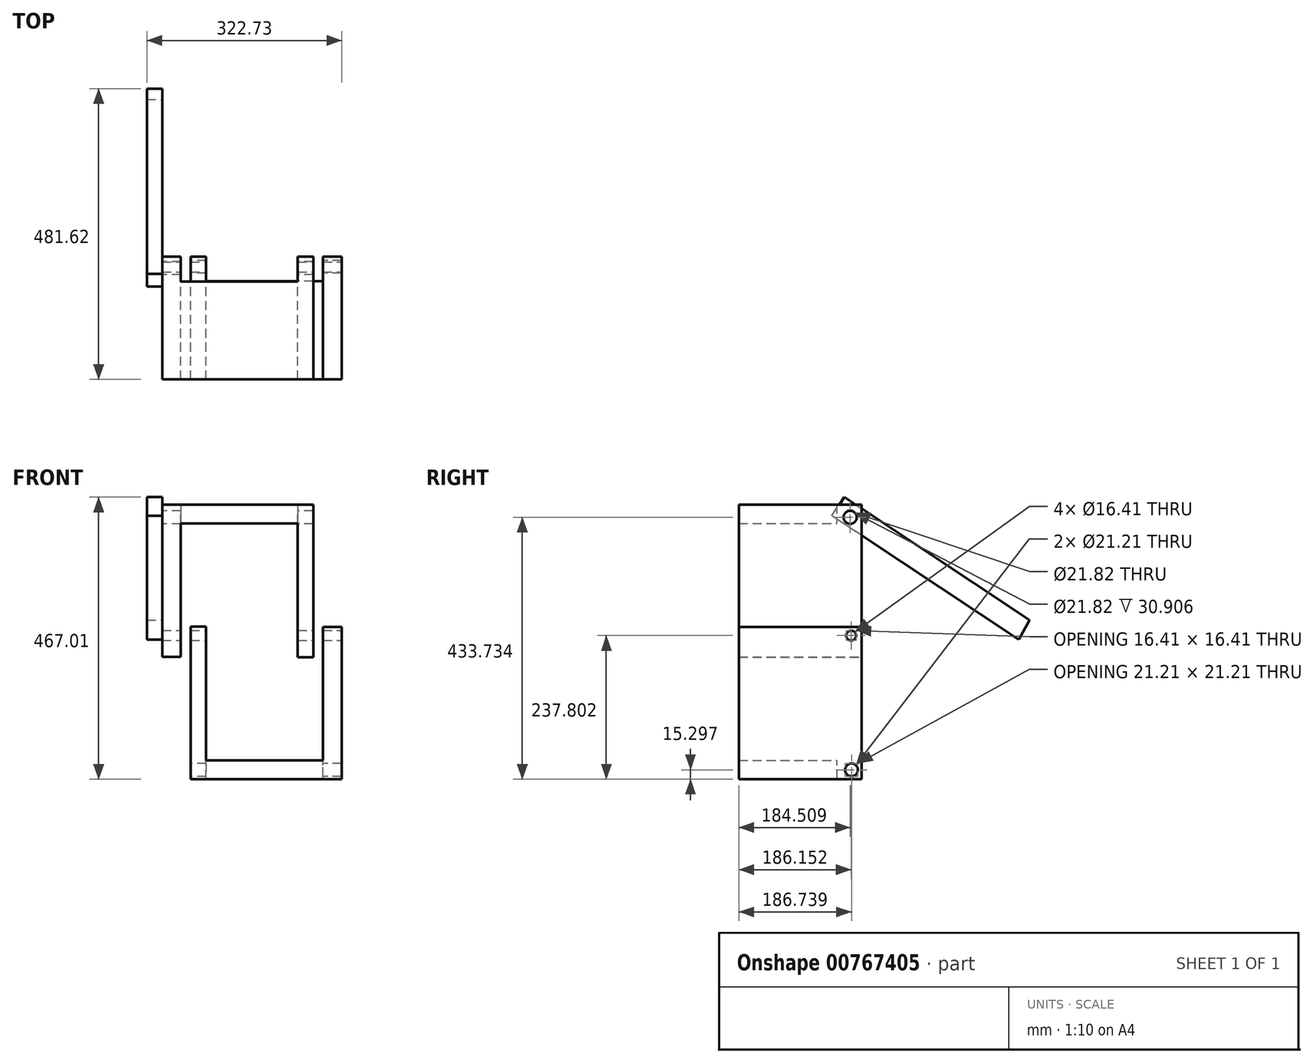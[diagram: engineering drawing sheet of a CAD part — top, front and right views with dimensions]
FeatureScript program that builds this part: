
annotation { "Feature Type Name" : "Feature", "Feature Type Description" : "" }
export const myFeature = defineFeature(function(context is Context, id is Id, definition is map)
    precondition{}
    {
        {
            var Q0;
            Q0=qCreatedBy(makeId("Front.planeOp"),FACE);
            var sketch = newSketch(context, id + "F0", { "sketchPlane" : qUnion([Q0])});
            skLineSegment(sketch, "E0", {"start": v(-82.01, 34.88) * mm, "end": v(-82.01, -217.77) * mm});
            skLineSegment(sketch, "E1", {"start": v(-82.01, -217.77) * mm, "end": v(168.25, -217.77) * mm});
            skLineSegment(sketch, "E2", {"start": v(168.25, -217.77) * mm, "end": v(168.25, 34.28) * mm});
            skLineSegment(sketch, "E3", {"start": v(168.25, 34.28) * mm, "end": v(137.35, 34.28) * mm});
            skLineSegment(sketch, "E4", {"start": v(137.35, 34.28) * mm, "end": v(137.35, -186.86) * mm});
            skLineSegment(sketch, "E5", {"start": v(137.35, -186.86) * mm, "end": v(-56.22, -186.86) * mm});
            skLineSegment(sketch, "E6", {"start": v(-56.22, -186.86) * mm, "end": v(-56.22, 34.88) * mm});
            skLineSegment(sketch, "E7", {"start": v(-56.22, 34.88) * mm, "end": v(-82.01, 34.88) * mm});
            skSolve(sketch);
        }
        {
            var Q0;
            Q0 = qSketchRegion(id + "F0", true);
            extrude(context, id + "F1", {"entities" : qUnion([Q0]), "depth" : 203.2 * mm, "offsetDistance" : 25.4 * mm});
        }
        {
            var Q0;
            Q0=makeQuery(id+"F1.opExtrude","SWEPT_BODY",BODY,{"disambiguationData":[OSD([sQuery(id+"F0.wireOp",EDGE,"E0"),sQuery(id+"F0.wireOp",EDGE,"E1"),sQuery(id+"F0.wireOp",EDGE,"E2"),sQuery(id+"F0.wireOp",EDGE,"E3"),sQuery(id+"F0.wireOp",EDGE,"E4"),sQuery(id+"F0.wireOp",EDGE,"E5"),sQuery(id+"F0.wireOp",EDGE,"E6"),sQuery(id+"F0.wireOp",EDGE,"E7")])]});
            transform(context, id + "F2", {"entities" : qUnion([Q0]), "transformType" : TransformType.TRANSLATION_3D, "dx" : 254 * mm, "dy" : 0 * mm, "dz" : 0 * mm, "makeCopy" : true});
        }
        {
            var Q0;
            Q0=makeQuery(id+"F2.opPattern","COPY",BODY,{"derivedFrom":makeQuery(id+"F1.opExtrude","SWEPT_BODY",BODY,{"disambiguationData":[OSD([sQuery(id+"F0.wireOp",EDGE,"E0"),sQuery(id+"F0.wireOp",EDGE,"E1"),sQuery(id+"F0.wireOp",EDGE,"E2"),sQuery(id+"F0.wireOp",EDGE,"E3"),sQuery(id+"F0.wireOp",EDGE,"E4"),sQuery(id+"F0.wireOp",EDGE,"E5"),sQuery(id+"F0.wireOp",EDGE,"E6"),sQuery(id+"F0.wireOp",EDGE,"E7")])]}),"instanceName":"1"});
            var Q1;
            Q1=makeQuery(id+"F2.opPattern","COPY",EDGE,{"derivedFrom":makeQuery(id+"F1.opExtrude","SWEPT_EDGE",EDGE,{"disambiguationData":[OSD([sQuery(id+"F0.wireOp",EDGE,"E0"),sQuery(id+"F0.wireOp",EDGE,"E7")])]}),"instanceName":"1"});
            transform(context, id + "F3", {"entities" : qUnion([Q0]), "transformType" : TransformType.ROTATION, "transformAxis" : qUnion([Q1]), "angle" : 180 * degree, "makeCopy" : false});
        }
        {
            var Q0;
            Q0=makeQuery(id+"F2.opPattern","COPY",BODY,{"derivedFrom":makeQuery(id+"F1.opExtrude","SWEPT_BODY",BODY,{"disambiguationData":[OSD([sQuery(id+"F0.wireOp",EDGE,"E0"),sQuery(id+"F0.wireOp",EDGE,"E1"),sQuery(id+"F0.wireOp",EDGE,"E2"),sQuery(id+"F0.wireOp",EDGE,"E3"),sQuery(id+"F0.wireOp",EDGE,"E4"),sQuery(id+"F0.wireOp",EDGE,"E5"),sQuery(id+"F0.wireOp",EDGE,"E6"),sQuery(id+"F0.wireOp",EDGE,"E7")])]}),"instanceName":"1"});
            var Q1;
            Q1=makeQuery(id+"F2.opPattern","COPY",EDGE,{"derivedFrom":makeQuery(id+"F1.opExtrude","CAP_EDGE",EDGE,{"disambiguationData":[OSD([sQuery(id+"F0.wireOp",EDGE,"E6")])],"isStart":true}),"instanceName":"1"});
            var Q2;
            Q2=makeQuery(id+"F2.opPattern","COPY",EDGE,{"derivedFrom":makeQuery(id+"F1.opExtrude","CAP_EDGE",EDGE,{"disambiguationData":[OSD([sQuery(id+"F0.wireOp",EDGE,"E6")])],"isStart":true}),"instanceName":"1"});
            transform(context, id + "F4", {"entities" : qUnion([Q0]), "transformType" : TransformType.TRANSLATION_DISTANCE, "transformDirection" : qUnion([Q2]), "distance" : 50.8 * mm, "makeCopy" : false});
        }
        {
            var Q0;
            Q0=makeQuery(id+"F2.opPattern","COPY",BODY,{"derivedFrom":makeQuery(id+"F1.opExtrude","SWEPT_BODY",BODY,{"disambiguationData":[OSD([sQuery(id+"F0.wireOp",EDGE,"E0"),sQuery(id+"F0.wireOp",EDGE,"E1"),sQuery(id+"F0.wireOp",EDGE,"E2"),sQuery(id+"F0.wireOp",EDGE,"E3"),sQuery(id+"F0.wireOp",EDGE,"E4"),sQuery(id+"F0.wireOp",EDGE,"E5"),sQuery(id+"F0.wireOp",EDGE,"E6"),sQuery(id+"F0.wireOp",EDGE,"E7")])]}),"instanceName":"1"});
            var Q1;
            Q1=makeQuery(id+"F2.opPattern","COPY",EDGE,{"derivedFrom":makeQuery(id+"F1.opExtrude","CAP_EDGE",EDGE,{"disambiguationData":[OSD([sQuery(id+"F0.wireOp",EDGE,"E1")])],"isStart":true}),"instanceName":"1"});
            transform(context, id + "F5", {"entities" : qUnion([Q0]), "transformType" : TransformType.TRANSLATION_DISTANCE, "transformDirection" : qUnion([Q1]), "distance" : 50.8 * mm, "makeCopy" : false});
        }
        {
            var Q0;
            Q0=makeQuery(id+"F1.opExtrude","SWEPT_FACE",FACE,{"disambiguationData":[OSD([sQuery(id+"F0.wireOp",EDGE,"E2")])]});
            var sketch = newSketch(context, id + "F6", { "sketchPlane" : qUnion([Q0])});
            skCircle(sketch, "E8", {"center": v(-17.05, 20.03) * mm, "radius": 8.2 * mm});
            skSolve(sketch);
        }
        {
            var Q0;
            Q0 = qSketchRegion(id + "F6", true);
            extrude(context, id + "F7", {"entities" : qUnion([Q0]), "operationType" : NewBodyOperationType.REMOVE, "endBound" : BoundingType.THROUGH_ALL, "oppositeDirection" : true, "depth" : 25.4 * mm, "offsetDistance" : 25.4 * mm});
        }
        {
            var Q0;
            Q0=makeQuery(id+"F2.opPattern","COPY",FACE,{"derivedFrom":makeQuery(id+"F1.opExtrude","SWEPT_FACE",FACE,{"disambiguationData":[OSD([sQuery(id+"F0.wireOp",EDGE,"E5")])]}),"instanceName":"1"});
            var sketch = newSketch(context, id + "F8", { "sketchPlane" : qUnion([Q0])});
            skLineSegment(sketch, "E9.bottom", {"start": v(95.4, 0) * mm, "end": v(-98.17, 0) * mm});
            skLineSegment(sketch, "E9.top", {"start": v(95.4, 41.25) * mm, "end": v(-98.17, 41.25) * mm});
            skLineSegment(sketch, "E9.left", {"start": v(95.4, 0) * mm, "end": v(95.4, 41.25) * mm});
            skLineSegment(sketch, "E9.right", {"start": v(-98.17, 0) * mm, "end": v(-98.17, 41.25) * mm});
            skSolve(sketch);
        }
        {
            var Q0;
            Q0=makeQuery(id+"F8.imprint","IMPRINT",FACE,{"disambiguationData":[TD([[makeQuery(id+"F8.imprint","IMPRINT",EDGE,{"derivedFrom":sQuery(id+"F8.wireOp",EDGE,"E9.bottom")}),1.0]])]});
            extrude(context, id + "F9", {"entities" : qUnion([Q0]), "operationType" : NewBodyOperationType.REMOVE, "endBound" : BoundingType.THROUGH_ALL, "oppositeDirection" : true, "depth" : 25.4 * mm, "offsetDistance" : 25.4 * mm});
        }
        {
            var Q0;
            Q0=makeQuery(id+"F1.opExtrude","SWEPT_FACE",FACE,{"disambiguationData":[OSD([sQuery(id+"F0.wireOp",EDGE,"E5")])]});
            var sketch = newSketch(context, id + "F10", { "sketchPlane" : qUnion([Q0])});
            skLineSegment(sketch, "E10.bottom", {"start": v(137.35, 0) * mm, "end": v(-56.22, 0) * mm});
            skLineSegment(sketch, "E10.top", {"start": v(137.35, -40.3) * mm, "end": v(-56.22, -40.3) * mm});
            skLineSegment(sketch, "E10.left", {"start": v(137.35, 0) * mm, "end": v(137.35, -40.3) * mm});
            skLineSegment(sketch, "E10.right", {"start": v(-56.22, 0) * mm, "end": v(-56.22, -40.3) * mm});
            skSolve(sketch);
        }
        {
            var Q0;
            Q0=makeQuery(id+"F10.imprint","IMPRINT",FACE,{"disambiguationData":[TD([[makeQuery(id+"F10.imprint","IMPRINT",EDGE,{"derivedFrom":sQuery(id+"F10.wireOp",EDGE,"E10.bottom")}),1.0]])]});
            extrude(context, id + "F11", {"entities" : qUnion([Q0]), "operationType" : NewBodyOperationType.REMOVE, "endBound" : BoundingType.THROUGH_ALL, "oppositeDirection" : true, "depth" : 25.4 * mm, "offsetDistance" : 25.4 * mm});
        }
        {
            var Q0;
            Q0=makeQuery(id+"F2.opPattern","COPY",FACE,{"derivedFrom":makeQuery(id+"F1.opExtrude","SWEPT_FACE",FACE,{"disambiguationData":[OSD([sQuery(id+"F0.wireOp",EDGE,"E2")])]}),"instanceName":"1"});
            var sketch = newSketch(context, id + "F12", { "sketchPlane" : qUnion([Q0])});
            skCircle(sketch, "E11", {"center": v(18.7, 215.96) * mm, "radius": 10.91 * mm});
            skCircle(sketch, "E12", {"center": v(16.46, -202.47) * mm, "radius": 10.6 * mm});
            skSolve(sketch);
        }
        {
            var Q0;
            Q0 = qSketchRegion(id + "F12", true);
            extrude(context, id + "F13", {"entities" : qUnion([Q0]), "operationType" : NewBodyOperationType.REMOVE, "endBound" : BoundingType.THROUGH_ALL, "oppositeDirection" : true, "depth" : 25.4 * mm, "offsetDistance" : 25.4 * mm});
        }
        {
            var Q0;
            Q0=makeQuery(id+"F2.opPattern","COPY",FACE,{"derivedFrom":makeQuery(id+"F1.opExtrude","SWEPT_FACE",FACE,{"disambiguationData":[OSD([sQuery(id+"F0.wireOp",EDGE,"E2")])]}),"instanceName":"1"});
            var sketch = newSketch(context, id + "F14", { "sketchPlane" : qUnion([Q0])});
            skLineSegment(sketch, "E13", {"start": v(-260.46, 13.34) * mm, "end": v(48.98, 218.29) * mm});
            skLineSegment(sketch, "E14", {"start": v(48.98, 218.29) * mm, "end": v(28.48, 249.24) * mm});
            skLineSegment(sketch, "E15", {"start": v(28.48, 249.24) * mm, "end": v(-278.42, 45.97) * mm});
            skLineSegment(sketch, "E16", {"start": v(-278.42, 45.97) * mm, "end": v(-260.46, 13.34) * mm});
            skSolve(sketch);
        }
        {
            var Q0;
            Q0 = qSketchRegion(id + "F14", true);
            extrude(context, id + "F15", {"entities" : qUnion([Q0]), "operationType" : NewBodyOperationType.ADD, "depth" : 25.4 * mm, "offsetDistance" : 25.4 * mm});
        }
    });
